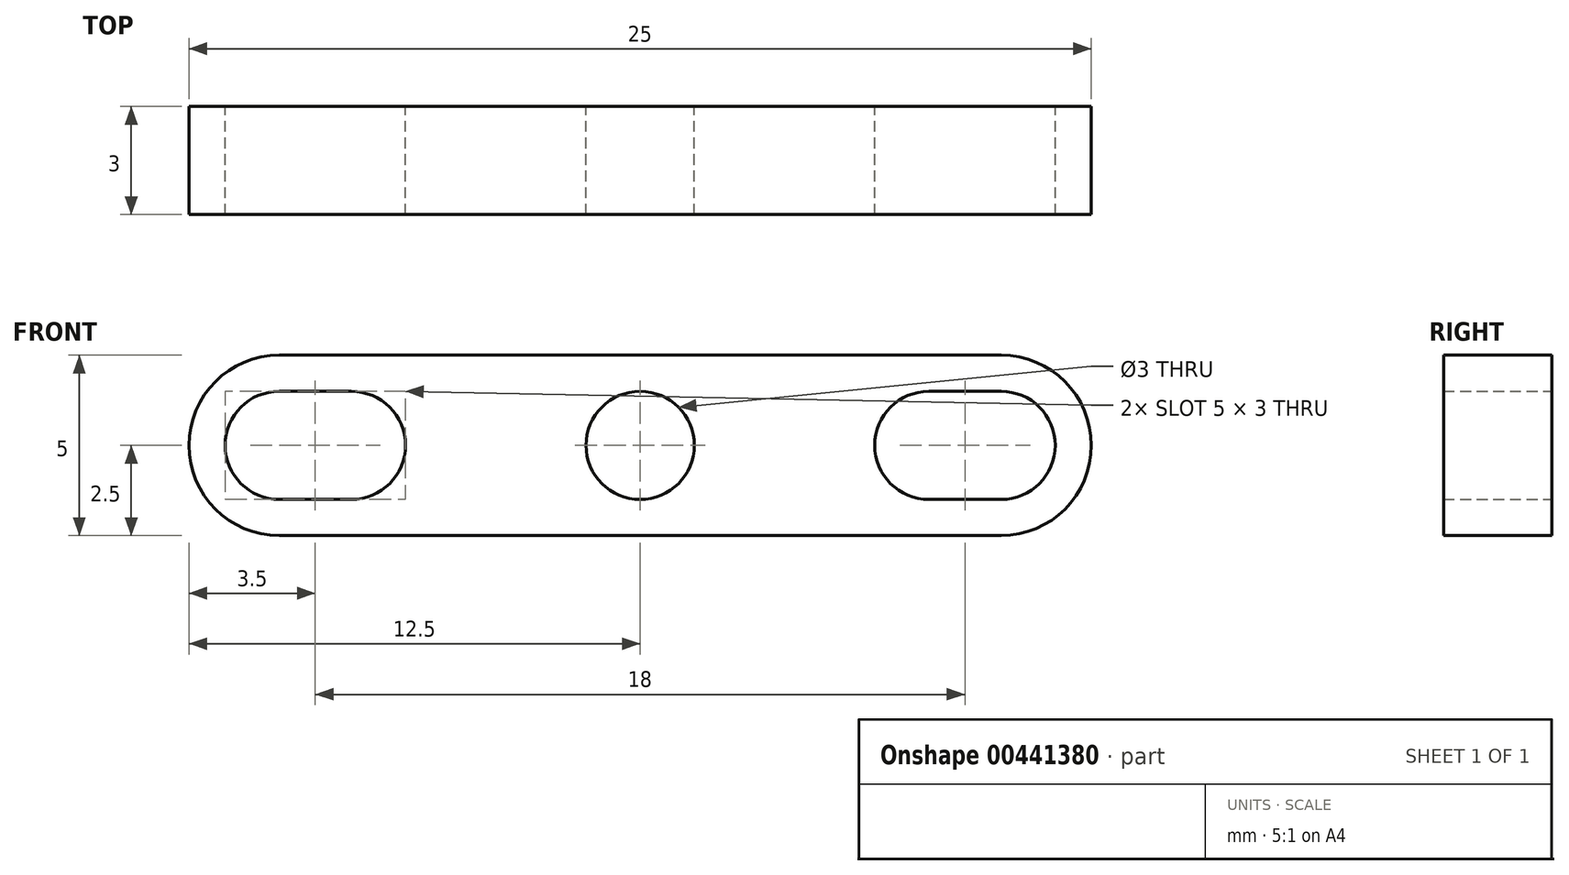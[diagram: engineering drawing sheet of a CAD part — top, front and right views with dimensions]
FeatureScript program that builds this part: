
annotation { "Feature Type Name" : "Feature", "Feature Type Description" : "" }
export const myFeature = defineFeature(function(context is Context, id is Id, definition is map)
    precondition{}
    {
        {
            var Q0;
            Q0=qCreatedBy(makeId("Front.planeOp"),FACE);
            var sketch = newSketch(context, id + "F0", { "sketchPlane" : qUnion([Q0])});
            skLineSegment(sketch, "E0.bottom", {"start": v(10, 2.5) * mm, "end": v(-10, 2.5) * mm});
            skLineSegment(sketch, "E0.top", {"start": v(10, -2.5) * mm, "end": v(-10, -2.5) * mm});
            skLineSegment(sketch, "E0.left", {"start": v(12.5, 0) * mm, "end": v(12.5, 0) * mm});
            skLineSegment(sketch, "E0.right", {"start": v(-12.5, 0) * mm, "end": v(-12.5, 0) * mm});
            skPoint(sketch, "E0.middle", {"position": v(0, 0) * mm});
            skCircle(sketch, "E1", {"center": v(0, 0) * mm, "radius": 1.5 * mm});
            skArc(sketch, "E2", {"start": v(-8, -1.5) * mm, "mid": v(-6.5, 0) * mm, "end": v(-8, 1.5) * mm});
            skArc(sketch, "E3", {"start": v(-10, 1.5) * mm, "mid": v(-11.5, 0) * mm, "end": v(-10, -1.5) * mm});
            skLineSegment(sketch, "E4", {"start": v(-10, 1.5) * mm, "end": v(-8, 1.5) * mm});
            skLineSegment(sketch, "E5", {"start": v(-10, -1.5) * mm, "end": v(-8, -1.5) * mm});
            skLineSegment(sketch, "E6.MirrorCS", {"start": v(10, -1.5) * mm, "end": v(8, -1.5) * mm});
            skArc(sketch, "E7.MirrorCS", {"start": v(8, -1.5) * mm, "mid": v(6.5, 0) * mm, "end": v(8, 1.5) * mm});
            skLineSegment(sketch, "E8.MirrorCS", {"start": v(10, 1.5) * mm, "end": v(8, 1.5) * mm});
            skArc(sketch, "E9.MirrorCS", {"start": v(10, 1.5) * mm, "mid": v(11.5, 0) * mm, "end": v(10, -1.5) * mm});
            skPoint(sketch, "E10.visualSharp", {"position": v(-12.5, 2.5) * mm});
            skArc(sketch, "E10.filletArc", {"start": v(-10, 2.5) * mm, "mid": v(-11.77, 1.77) * mm, "end": v(-12.5, 0) * mm});
            skPoint(sketch, "E11.visualSharp", {"position": v(-12.5, -2.5) * mm});
            skArc(sketch, "E11.filletArc", {"start": v(-12.5, 0) * mm, "mid": v(-11.77, -1.77) * mm, "end": v(-10, -2.5) * mm});
            skPoint(sketch, "E12.visualSharp", {"position": v(12.5, -2.5) * mm});
            skArc(sketch, "E12.filletArc", {"start": v(10, -2.5) * mm, "mid": v(11.77, -1.77) * mm, "end": v(12.5, 0) * mm});
            skPoint(sketch, "E13.visualSharp", {"position": v(12.5, 2.5) * mm});
            skArc(sketch, "E13.filletArc", {"start": v(12.5, 0) * mm, "mid": v(11.77, 1.77) * mm, "end": v(10, 2.5) * mm});
            skSolve(sketch);
        }
        {
            var Q0;
            Q0 = qSketchRegion(id + "F0", true);
            extrude(context, id + "F1", {"entities" : qUnion([Q0]), "depth" : 3 * mm});
        }
    });
